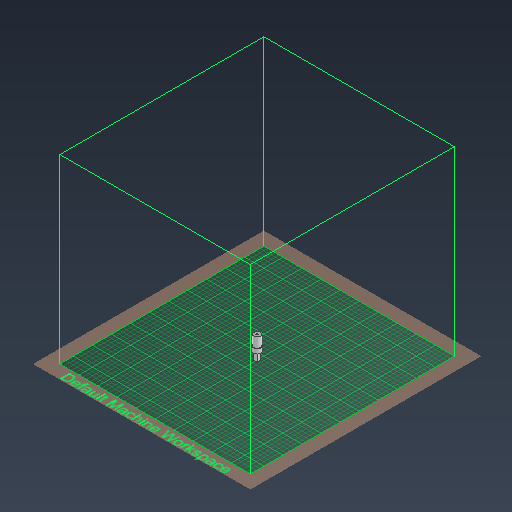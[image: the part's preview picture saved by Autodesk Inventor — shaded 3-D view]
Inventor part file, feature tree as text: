
AUTODESK INVENTOR PART (.ipt)
format: ipt  version: 2021 (Build 250183000, 183)  size: 270,848 bytes
history: native  units: mm
features: extrude x5, sketch x5, other x1
ambient origin geometry x8: Origin, YZ Plane, XZ Plane, XY Plane, X Axis, Y Axis, Z Axis, Center Point
bodies: Volumenkörper1 (feature_tree)
feature tree (11):
  other  "Boogie_Stange"
  extrude  "Extrusion1"  Depth=22.0mm TaperAngle=0.0deg
  extrude  "Extrusion2"  Depth=10.0mm TaperAngle=0.0deg
  extrude  "Extrusion3"  Depth=8.5mm
  extrude  "Extrusion4"  Depth=17.4mm
  extrude  "Extrusion5"  Depth=5.0mm
  sketch  "Skizze1"  dims[d0=14.8mm d1=22.0mm d2=0.0mm]
  sketch  "Skizze2"  dims[d3=17.0mm d4=10.0mm d5=0.0mm]
  sketch  "Skizze3"  dims[d6=8.5mm d7=8.5mm]
  sketch  "Skizze4"  dims[d8=17.4mm d9=0.0mm d10=4.0mm]
  sketch  "Skizze5"  dims[d11=5.0mm d12=0.0mm d13=4.0mm d14=5.0mm d15=0.0mm]
